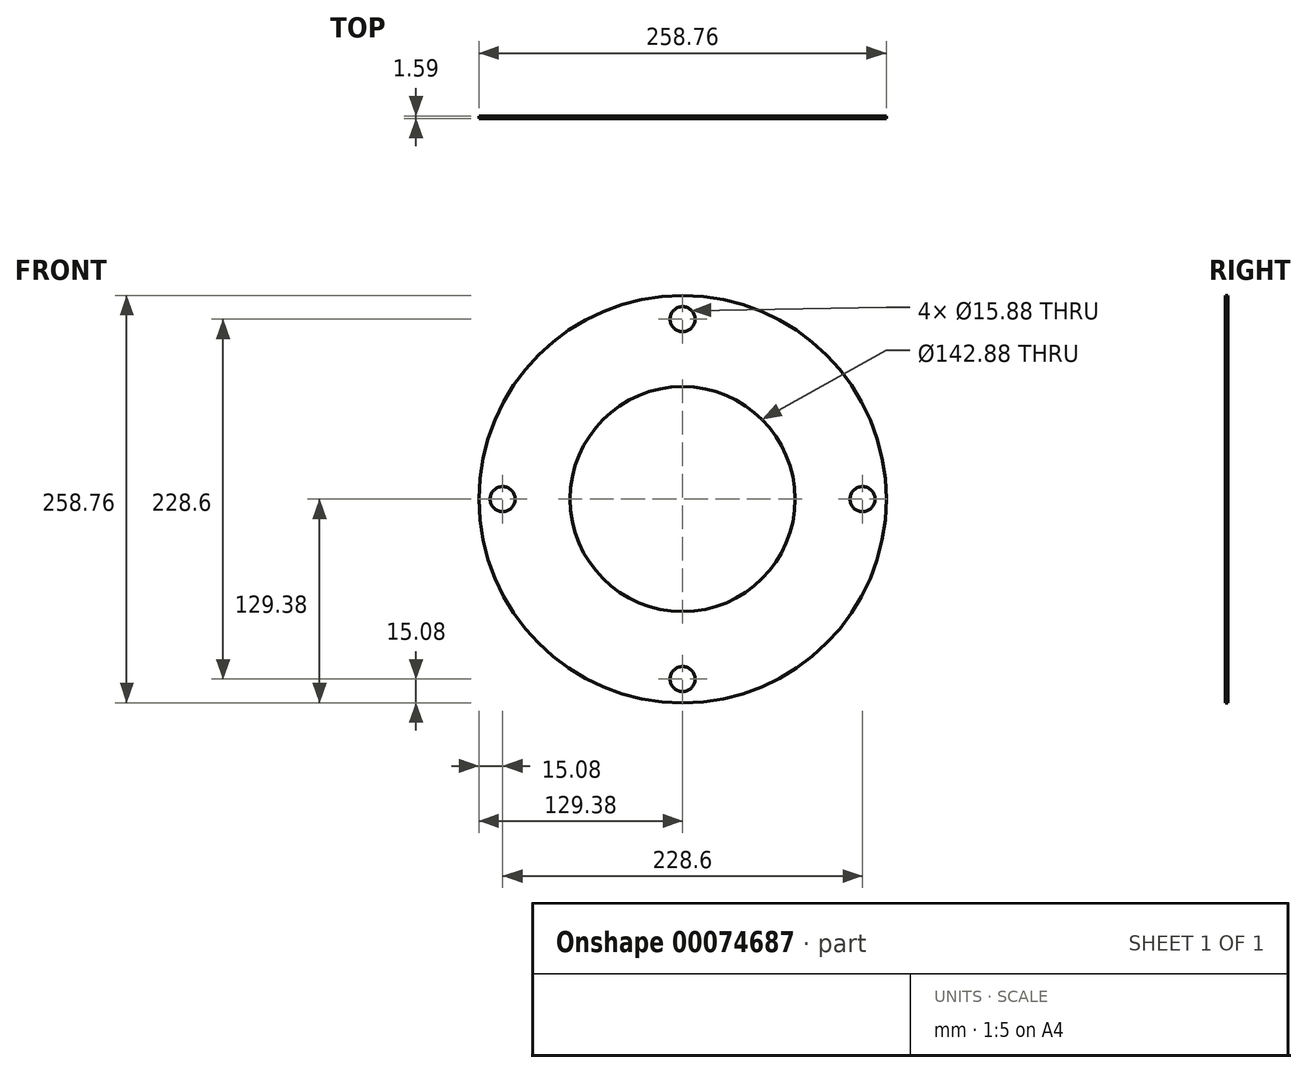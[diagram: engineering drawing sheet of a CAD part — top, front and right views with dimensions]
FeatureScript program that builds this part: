
annotation { "Feature Type Name" : "Feature", "Feature Type Description" : "" }
export const myFeature = defineFeature(function(context is Context, id is Id, definition is map)
    precondition{}
    {
        {
            var Q0;
            Q0=qCreatedBy(makeId("Front.planeOp"),FACE);
            var sketch = newSketch(context, id + "F0", { "sketchPlane" : qUnion([Q0])});
            skCircle(sketch, "E0", {"center": v(0, 0) * mm, "radius": 129.38 * mm});
            skCircle(sketch, "E1", {"center": v(0, 0) * mm, "radius": 71.44 * mm});
            skCircle(sketch, "E2", {"center": v(0, 114.3) * mm, "radius": 7.94 * mm});
            skCircle(sketch, "E3.1.0", {"center": v(-114.3, 0) * mm, "radius": 7.94 * mm});
            skCircle(sketch, "E3.2.0", {"center": v(0, -114.3) * mm, "radius": 7.94 * mm});
            skCircle(sketch, "E3.3.0", {"center": v(114.3, 0) * mm, "radius": 7.94 * mm});
            skSolve(sketch);
        }
        {
            var Q0;
            Q0=makeQuery(id+"F0.imprint","IMPRINT",FACE,{"disambiguationData":[TD([[makeQuery(id+"F0.imprint","IMPRINT",EDGE,{"derivedFrom":sQuery(id+"F0.wireOp",EDGE,"E0")}),1.0]])]});
            extrude(context, id + "F1", {"entities" : qUnion([Q0]), "depth" : 1.59 * mm});
        }
    });
